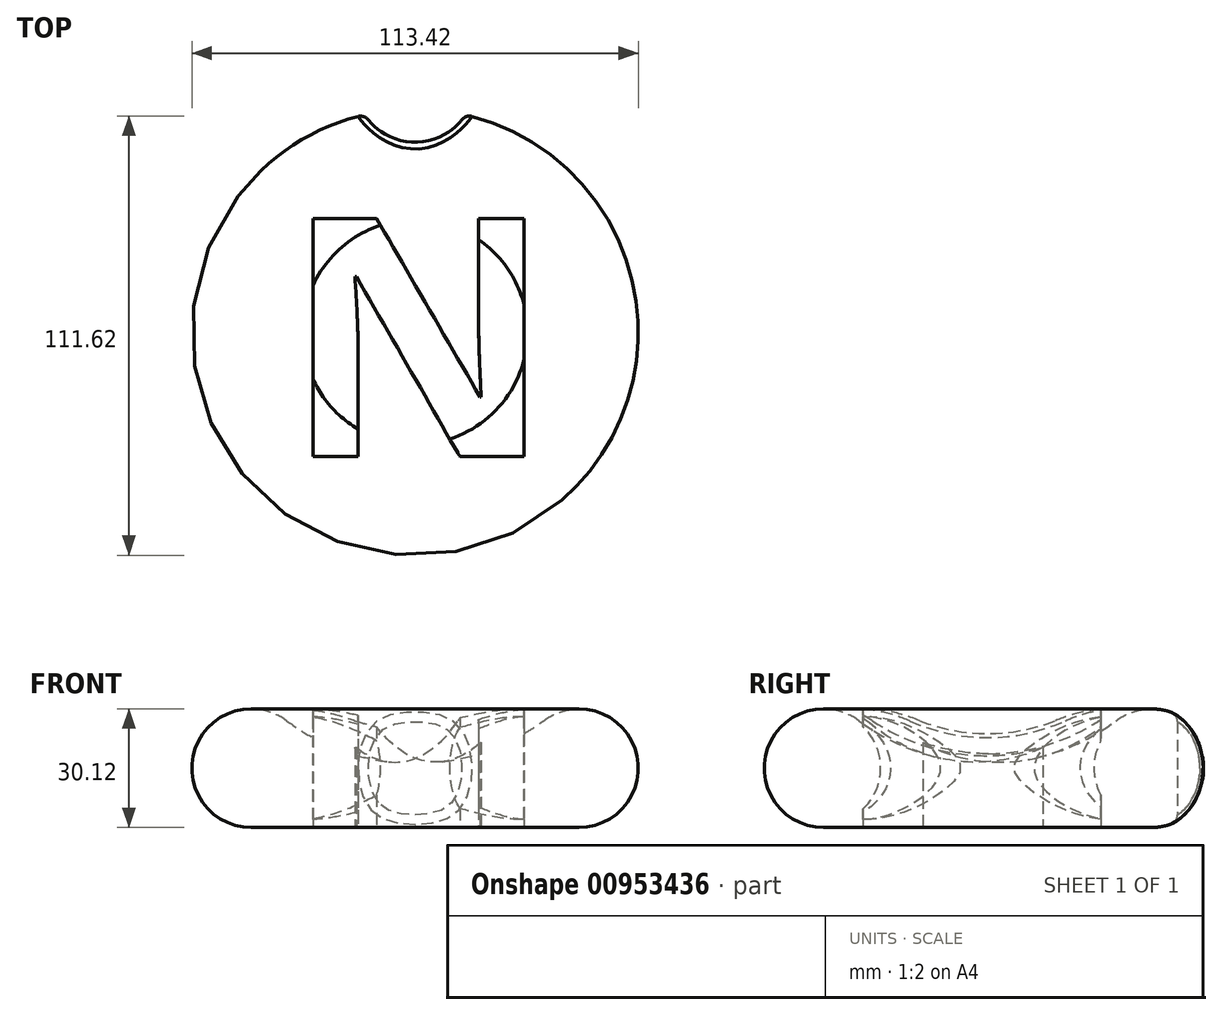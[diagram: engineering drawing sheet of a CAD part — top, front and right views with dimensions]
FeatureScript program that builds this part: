
annotation { "Feature Type Name" : "Feature", "Feature Type Description" : "" }
export const myFeature = defineFeature(function(context is Context, id is Id, definition is map)
    precondition{}
    {
        {
            var Q0;
            Q0=qCreatedBy(makeId("Front.planeOp"),FACE);
            var sketch = newSketch(context, id + "F0", { "sketchPlane" : qUnion([Q0])});
            skArc(sketch, "E0", {"start": v(-32.63, 27.11) * mm, "mid": v(-55.94, 19.82) * mm, "end": v(-41.65, 0) * mm});
            skArc(sketch, "E1", {"start": v(-32.63, 27.11) * mm, "mid": v(-17.2, 19.04) * mm, "end": v(0, 16.25) * mm});
            skLineSegment(sketch, "E2", {"start": v(0, 0) * mm, "end": v(-41.65, 0) * mm});
            skLineSegment(sketch, "E3", {"start": v(0, 0) * mm, "end": v(0, 16.25) * mm});
            skSolve(sketch);
        }
        {
            var Q0;
            Q0=makeQuery(id+"F0.imprint","IMPRINT",FACE,{"disambiguationData":[TD([[makeQuery(id+"F0.imprint","IMPRINT",EDGE,{"derivedFrom":sQuery(id+"F0.wireOp",EDGE,"E0")}),1.0]])]});
            var Q1;
            Q1=sQuery(id+"F0.wireOp",EDGE,"E3");
            revolve(context, id + "F1", {"surfaceOperationType" : NewSurfaceOperationType.NEW, "entities" : qUnion([Q0]), "axis" : qUnion([Q1]), "revolveType" : RevolveType.FULL});
        }
        {
            var Q0;
            Q0=qCreatedBy(makeId("Top.planeOp"),FACE);
            var sketch = newSketch(context, id + "F2", { "sketchPlane" : qUnion([Q0])});
            skCircle(sketch, "E4", {"center": v(0, 63.5) * mm, "radius": 15.24 * mm});
            skSolve(sketch);
        }
        {
            var Q0;
            Q0 = qSketchRegion(id + "F2", true);
            extrude(context, id + "F3", {"entities" : qUnion([Q0]), "operationType" : NewBodyOperationType.REMOVE, "depth" : 41.66 * mm, "offsetDistance" : 25.4 * mm});
        }
        {
            var Q0;
            Q0=makeQuery(id+"F3.boolean.opBoolean","INTERSECT",EDGE,{"derivedFrom":[makeQuery(id+"F1.opRevolve","SWEPT_FACE",FACE,{"disambiguationData":[OSD([sQuery(id+"F0.wireOp",EDGE,"E0")])]}),makeQuery(id+"F3.opExtrude","SWEPT_FACE",FACE,{"disambiguationData":[OSD([sQuery(id+"F2.wireOp",EDGE,"E4")])]})]});
            fillet(context, id + "F4", {"entities" : qUnion([Q0]), "radius" : 2.54 * mm, "tangentPropagation" : true, "allowEdgeOverflow" : false});
        }
        {
            var Q0;
            Q0=qCreatedBy(makeId("Top.planeOp"),FACE);
            var sketch = newSketch(context, id + "F5", { "sketchPlane" : qUnion([Q0])});
            skText(sketch, "E5", { "text": "N", "fontName": "OpenSans-Bold.ttf"});
            const initialGuessF5  = {"E5": [-0.03357, -0.03163, 1, 0, 0.06103]};
            skSetInitialGuess(sketch, initialGuessF5);
            skSolve(sketch);
        }
        {
            var Q0;
            Q0 = qSketchRegion(id + "F5", true);
            extrude(context, id + "F6", {"entities" : qUnion([Q0]), "operationType" : NewBodyOperationType.REMOVE, "depth" : 74.42 * mm, "offsetDistance" : 25.4 * mm});
        }
        {
            var Q0;
            Q0=qCreatedBy(makeId("Front.planeOp"),FACE);
            var sketch = newSketch(context, id + "F7", { "sketchPlane" : qUnion([Q0])});
            skArc(sketch, "E6", {"start": v(-45.24, 2.5) * mm, "mid": v(-28.54, 15.13) * mm, "end": v(-45.24, 27.75) * mm});
            skLineSegment(sketch, "E7", {"start": v(-45.24, 27.75) * mm, "end": v(-45.24, 2.5) * mm});
            skSolve(sketch);
        }
        {
            var Q0;
            Q0 = qSketchRegion(id + "F7", true);
            var Q1;
            Q1=sQuery(id+"F0.wireOp",EDGE,"E3");
            revolve(context, id + "F8", {"operationType" : NewBodyOperationType.ADD, "surfaceOperationType" : NewSurfaceOperationType.NEW, "entities" : qUnion([Q0]), "axis" : qUnion([Q1]), "revolveType" : RevolveType.FULL});
        }
    });
